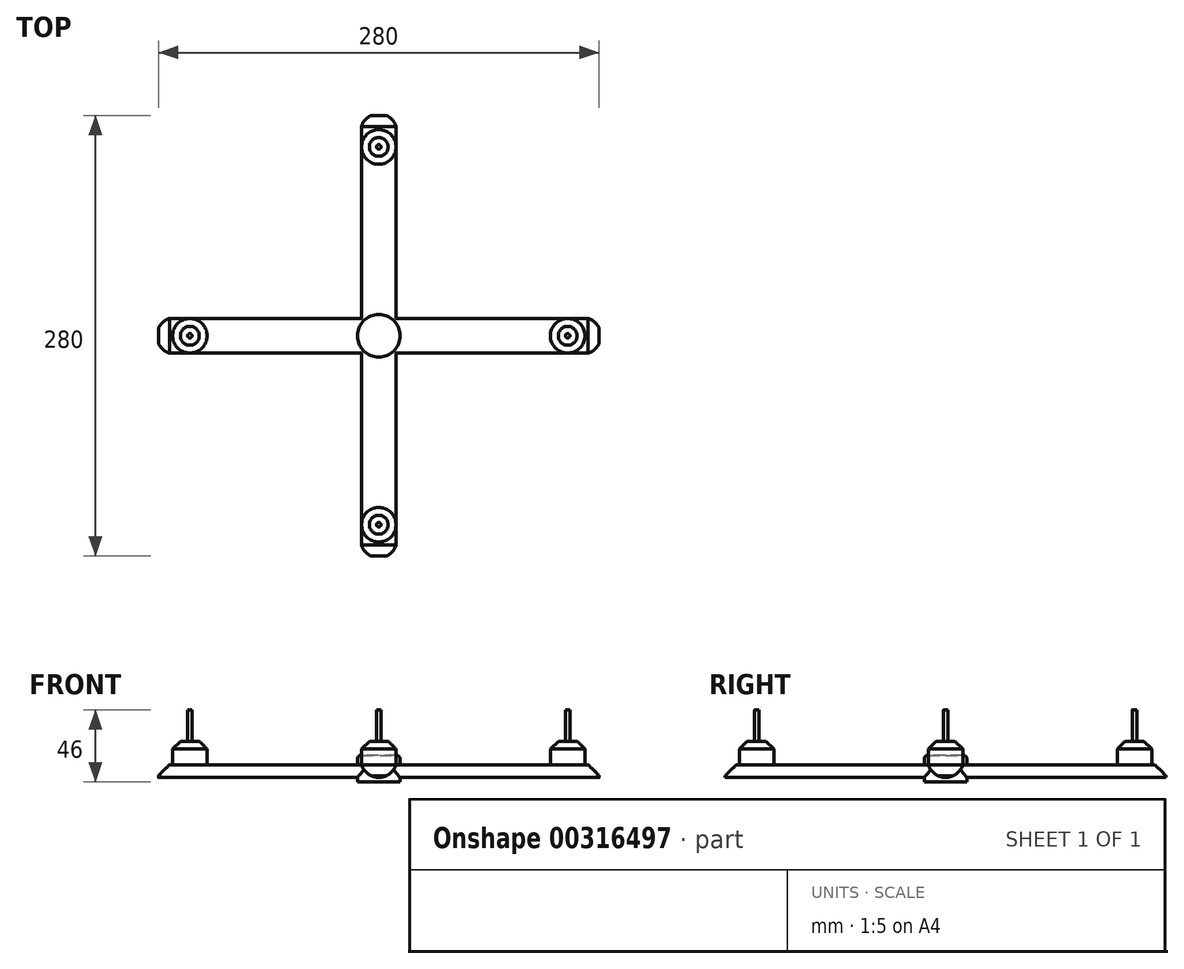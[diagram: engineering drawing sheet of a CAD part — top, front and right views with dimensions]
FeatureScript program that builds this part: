
annotation { "Feature Type Name" : "Feature", "Feature Type Description" : "" }
export const myFeature = defineFeature(function(context is Context, id is Id, definition is map)
    precondition{}
    {
        {
            var Q0;
            Q0=qCreatedBy(makeId("Top.planeOp"),FACE);
            var sketch = newSketch(context, id + "F0", { "sketchPlane" : qUnion([Q0])});
            skCircle(sketch, "E0", {"center": v(0, 0) * mm, "radius": 13.5 * mm});
            skSolve(sketch);
        }
        {
            var Q0;
            Q0=qCreatedBy(makeId("Front.planeOp"),FACE);
            var sketch = newSketch(context, id + "F1", { "sketchPlane" : qUnion([Q0])});
            skLineSegment(sketch, "E1.bottom", {"start": v(-11, 4) * mm, "end": v(11, 4) * mm});
            skLineSegment(sketch, "E1.top", {"start": v(-11, -4) * mm, "end": v(11, -4) * mm});
            skLineSegment(sketch, "E1.left", {"start": v(-11, 4) * mm, "end": v(-11, -4) * mm});
            skLineSegment(sketch, "E1.right", {"start": v(11, 4) * mm, "end": v(11, -4) * mm});
            skPoint(sketch, "E1.middle", {"position": v(0, 0) * mm});
            skSolve(sketch);
        }
        {
            var Q0;
            Q0=qCreatedBy(makeId("Right.planeOp"),FACE);
            var sketch = newSketch(context, id + "F2", { "sketchPlane" : qUnion([Q0])});
            skLineSegment(sketch, "E2.bottom", {"start": v(-11, 4) * mm, "end": v(11, 4) * mm});
            skLineSegment(sketch, "E2.top", {"start": v(-11, -4) * mm, "end": v(11, -4) * mm});
            skLineSegment(sketch, "E2.left", {"start": v(-11, 4) * mm, "end": v(-11, -4) * mm});
            skLineSegment(sketch, "E2.right", {"start": v(11, 4) * mm, "end": v(11, -4) * mm});
            skPoint(sketch, "E2.middle", {"position": v(0, 0) * mm});
            skSolve(sketch);
        }
        {
            var Q0;
            Q0=makeQuery(id+"F2.imprint","IMPRINT",FACE,{"disambiguationData":[TD([[makeQuery(id+"F2.imprint","IMPRINT",EDGE,{"derivedFrom":sQuery(id+"F2.wireOp",EDGE,"E2.bottom")}),-1.0]])]});
            extrude(context, id + "F3", {"entities" : qUnion([Q0]), "depth" : 140 * mm});
        }
        {
            var Q0;
            Q0=makeQuery(id+"F0.imprint","IMPRINT",FACE,{"disambiguationData":[TD([[makeQuery(id+"F0.imprint","IMPRINT",EDGE,{"derivedFrom":sQuery(id+"F0.wireOp",EDGE,"E0")}),1.0]])]});
            extrude(context, id + "F4", {"entities" : qUnion([Q0]), "operationType" : NewBodyOperationType.ADD, "depth" : 10 * mm});
        }
        {
            var Q0;
            Q0=makeQuery(id+"F1.imprint","IMPRINT",FACE,{"disambiguationData":[TD([[makeQuery(id+"F1.imprint","IMPRINT",EDGE,{"derivedFrom":sQuery(id+"F1.wireOp",EDGE,"E1.bottom")}),-1.0]])]});
            extrude(context, id + "F5", {"entities" : qUnion([Q0]), "operationType" : NewBodyOperationType.ADD, "depth" : 140 * mm});
        }
        {
            var Q0;
            Q0=makeQuery(id+"F2.imprint","IMPRINT",FACE,{"disambiguationData":[TD([[makeQuery(id+"F2.imprint","IMPRINT",EDGE,{"derivedFrom":sQuery(id+"F2.wireOp",EDGE,"E2.bottom")}),-1.0]])]});
            extrude(context, id + "F6", {"entities" : qUnion([Q0]), "operationType" : NewBodyOperationType.ADD, "depth" : -140 * mm});
        }
        {
            var Q0;
            Q0=makeQuery(id+"F1.imprint","IMPRINT",FACE,{"disambiguationData":[TD([[makeQuery(id+"F1.imprint","IMPRINT",EDGE,{"derivedFrom":sQuery(id+"F1.wireOp",EDGE,"E1.bottom")}),-1.0]])]});
            extrude(context, id + "F7", {"entities" : qUnion([Q0]), "operationType" : NewBodyOperationType.ADD, "depth" : -140 * mm});
        }
        {
            var Q0;
            Q0=makeQuery(id+"F0.imprint","IMPRINT",FACE,{"disambiguationData":[TD([[makeQuery(id+"F0.imprint","IMPRINT",EDGE,{"derivedFrom":sQuery(id+"F0.wireOp",EDGE,"E0")}),1.0]])]});
            extrude(context, id + "F8", {"entities" : qUnion([Q0]), "operationType" : NewBodyOperationType.ADD, "depth" : -7 * mm});
        }
        {
            var Q0;
            Q0=makeQuery(id+"F4.opExtrude","CAP_EDGE",EDGE,{"disambiguationData":[OSD([sQuery(id+"F0.wireOp",EDGE,"E0")])],"isStart":false});
            fillet(context, id + "F9", {"entities" : qUnion([Q0]), "radius" : 2.17 * mm, "tangentPropagation" : true, "allowEdgeOverflow" : false});
        }
        {
            var Q0;
            Q0=makeQuery(id+"F5.opExtrude","SWEPT_EDGE",EDGE,{"disambiguationData":[OSD([sQuery(id+"F1.wireOp",EDGE,"E1.top"),sQuery(id+"F1.wireOp",EDGE,"E1.right")])]});
            var Q1;
            Q1=makeQuery(id+"F5.opExtrude","SWEPT_EDGE",EDGE,{"disambiguationData":[OSD([sQuery(id+"F1.wireOp",EDGE,"E1.top"),sQuery(id+"F1.wireOp",EDGE,"E1.left")])]});
            var Q2;
            Q2=makeQuery(id+"F6.opExtrude","SWEPT_EDGE",EDGE,{"disambiguationData":[OSD([sQuery(id+"F2.wireOp",EDGE,"E2.top"),sQuery(id+"F2.wireOp",EDGE,"E2.left")])]});
            var Q3;
            {var subQ0=sQuery(id+"F2.wireOp",EDGE,"E2.right");var subQ1=sQuery(id+"F2.wireOp",EDGE,"E2.top");Q3=makeQuery(id+"F7.boolean.opBoolean","SPLIT",EDGE,{"disambiguationData":[TD([makeQuery(id+"F7.opExtrude","SWEPT_FACE",FACE,{"disambiguationData":[OSD([sQuery(id+"F1.wireOp",EDGE,"E1.left")])]})])],"derivedFrom":makeQuery(id+"F6.boolean.opBoolean","MERGE",EDGE,{"derivedFrom":[makeQuery(id+"F3.opExtrude","SWEPT_EDGE",EDGE,{"disambiguationData":[OSD([subQ1,subQ0])]}),makeQuery(id+"F6.opExtrude","SWEPT_EDGE",EDGE,{"disambiguationData":[OSD([subQ1,subQ0])]})]})});}
            var Q4;
            Q4=makeQuery(id+"F7.opExtrude","SWEPT_EDGE",EDGE,{"disambiguationData":[OSD([sQuery(id+"F1.wireOp",EDGE,"E1.top"),sQuery(id+"F1.wireOp",EDGE,"E1.left")])]});
            var Q5;
            Q5=makeQuery(id+"F7.opExtrude","SWEPT_EDGE",EDGE,{"disambiguationData":[OSD([sQuery(id+"F1.wireOp",EDGE,"E1.top"),sQuery(id+"F1.wireOp",EDGE,"E1.right")])]});
            var Q6;
            {var subQ1=sQuery(id+"F2.wireOp",EDGE,"E2.right");var subQ2=sQuery(id+"F2.wireOp",EDGE,"E2.top");Q6=makeQuery(id+"F7.boolean.opBoolean","SPLIT",EDGE,{"disambiguationData":[TD([makeQuery(id+"F7.opExtrude","SWEPT_FACE",FACE,{"disambiguationData":[OSD([sQuery(id+"F1.wireOp",EDGE,"E1.right")])]})])],"derivedFrom":makeQuery(id+"F6.boolean.opBoolean","MERGE",EDGE,{"derivedFrom":[makeQuery(id+"F3.opExtrude","SWEPT_EDGE",EDGE,{"disambiguationData":[OSD([subQ2,subQ1])]}),makeQuery(id+"F6.opExtrude","SWEPT_EDGE",EDGE,{"disambiguationData":[OSD([subQ2,subQ1])]})]})});}
            var Q7;
            Q7=makeQuery(id+"F3.opExtrude","SWEPT_EDGE",EDGE,{"disambiguationData":[OSD([sQuery(id+"F2.wireOp",EDGE,"E2.top"),sQuery(id+"F2.wireOp",EDGE,"E2.left")])]});
            fillet(context, id + "F10", {"entities" : qUnion([Q0, Q1, Q2, Q3, Q4, Q5, Q6, Q7]), "radius" : 11.5 * mm, "tangentPropagation" : true, "allowEdgeOverflow" : false});
        }
        {
            var Q0;
            {var subQ0=sQuery(id+"F1.wireOp",EDGE,"E1.bottom");var subQ1=sQuery(id+"F2.wireOp",EDGE,"E2.bottom");Q0=makeQuery(id+"F7.boolean.opBoolean","MERGE",FACE,{"derivedFrom":[makeQuery(id+"F6.boolean.opBoolean","MERGE",FACE,{"derivedFrom":[makeQuery(id+"F5.boolean.opBoolean","MERGE",FACE,{"derivedFrom":[makeQuery(id+"F3.opExtrude","SWEPT_FACE",FACE,{"disambiguationData":[OSD([subQ1])]}),makeQuery(id+"F5.opExtrude","SWEPT_FACE",FACE,{"disambiguationData":[OSD([subQ0])]})]}),makeQuery(id+"F6.opExtrude","SWEPT_FACE",FACE,{"disambiguationData":[OSD([subQ1])]})]}),makeQuery(id+"F7.opExtrude","SWEPT_FACE",FACE,{"disambiguationData":[OSD([subQ0])]})]});}
            var sketch = newSketch(context, id + "F11", { "sketchPlane" : qUnion([Q0])});
            skLineSegment(sketch, "E3", {"start": v(0, -140) * mm, "end": v(0, -120) * mm});
            skLineSegment(sketch, "E4", {"start": v(140, 0) * mm, "end": v(120, 0) * mm});
            skPoint(sketch, "E4.endSnap0", {"position": v(140, 0) * mm});
            skLineSegment(sketch, "E5", {"start": v(0, 140) * mm, "end": v(0, 120) * mm});
            skLineSegment(sketch, "E6", {"start": v(-140, 0) * mm, "end": v(-120, 0) * mm});
            skCircle(sketch, "E7", {"center": v(0, 120) * mm, "radius": 11 * mm});
            skCircle(sketch, "E8", {"center": v(120, 0) * mm, "radius": 11 * mm});
            skCircle(sketch, "E9", {"center": v(0, -120) * mm, "radius": 11 * mm});
            skCircle(sketch, "E10", {"center": v(-120, 0) * mm, "radius": 11 * mm});
            skSolve(sketch);
        }
        {
            var Q0;
            Q0=makeQuery(id+"F5.opExtrude","CAP_EDGE",EDGE,{"disambiguationData":[OSD([sQuery(id+"F1.wireOp",EDGE,"E1.bottom")])],"isStart":false});
            var Q1;
            Q1=makeQuery(id+"F3.opExtrude","CAP_EDGE",EDGE,{"disambiguationData":[OSD([sQuery(id+"F2.wireOp",EDGE,"E2.bottom")])],"isStart":false});
            var Q2;
            Q2=makeQuery(id+"F7.opExtrude","CAP_EDGE",EDGE,{"disambiguationData":[OSD([sQuery(id+"F1.wireOp",EDGE,"E1.bottom")])],"isStart":false});
            var Q3;
            Q3=makeQuery(id+"F6.opExtrude","CAP_EDGE",EDGE,{"disambiguationData":[OSD([sQuery(id+"F2.wireOp",EDGE,"E2.bottom")])],"isStart":false});
            chamfer(context, id + "F12", {"entities" : qUnion([Q0, Q1, Q2, Q3]), "width" : 7 * mm, "tangentPropagation" : true});
        }
        {
            var Q0;
            {var subQ0=sQuery(id+"F11.wireOp",EDGE,"E9");var subQ7=makeQuery(id+"F11.imprint","INTERSECT",VERTEX,{"derivedFrom":[sQuery(id+"F11.wireOp",EDGE,"E3"),subQ0]});Q0=makeQuery(id+"F11.imprint","IMPRINT",FACE,{"disambiguationData":[TD([[makeQuery(id+"F11.imprint","IMPRINT",EDGE,{"disambiguationData":[TD([[subQ7,1.0]])],"derivedFrom":subQ0}),1.0]])]});}
            var Q1;
            {var subQ0=sQuery(id+"F11.wireOp",EDGE,"E8");var subQ1=makeQuery(id+"F11.imprint","INTERSECT",VERTEX,{"derivedFrom":[sQuery(id+"F11.wireOp",EDGE,"E4"),subQ0]});Q1=makeQuery(id+"F11.imprint","IMPRINT",FACE,{"disambiguationData":[TD([[makeQuery(id+"F11.imprint","IMPRINT",EDGE,{"disambiguationData":[TD([[subQ1,1.0]])],"derivedFrom":subQ0}),1.0]])]});}
            var Q2;
            {var subQ0=sQuery(id+"F11.wireOp",EDGE,"E7");var subQ1=makeQuery(id+"F11.imprint","INTERSECT",VERTEX,{"derivedFrom":[sQuery(id+"F11.wireOp",EDGE,"E5"),subQ0]});Q2=makeQuery(id+"F11.imprint","IMPRINT",FACE,{"disambiguationData":[TD([[makeQuery(id+"F11.imprint","IMPRINT",EDGE,{"disambiguationData":[TD([[subQ1,1.0]])],"derivedFrom":subQ0}),1.0]])]});}
            var Q3;
            {var subQ0=sQuery(id+"F11.wireOp",EDGE,"E10");var subQ1=makeQuery(id+"F11.imprint","INTERSECT",VERTEX,{"derivedFrom":[sQuery(id+"F11.wireOp",EDGE,"E6"),subQ0]});Q3=makeQuery(id+"F11.imprint","IMPRINT",FACE,{"disambiguationData":[TD([[makeQuery(id+"F11.imprint","IMPRINT",EDGE,{"disambiguationData":[TD([[subQ1,-1.0]])],"derivedFrom":subQ0}),1.0]])]});}
            extrude(context, id + "F13", {"entities" : qUnion([Q0, Q1, Q2, Q3]), "operationType" : NewBodyOperationType.ADD, "depth" : 15 * mm});
        }
        {
            var Q0;
            Q0=makeQuery(id+"F13.opExtrude","CAP_EDGE",EDGE,{"disambiguationData":[OSD([sQuery(id+"F11.wireOp",EDGE,"E9")])],"isStart":false});
            var Q1;
            Q1=makeQuery(id+"F13.opExtrude","CAP_EDGE",EDGE,{"disambiguationData":[OSD([sQuery(id+"F11.wireOp",EDGE,"E8")])],"isStart":false});
            var Q2;
            Q2=makeQuery(id+"F13.opExtrude","CAP_EDGE",EDGE,{"disambiguationData":[OSD([sQuery(id+"F11.wireOp",EDGE,"E7")])],"isStart":false});
            var Q3;
            Q3=makeQuery(id+"F13.opExtrude","CAP_EDGE",EDGE,{"disambiguationData":[OSD([sQuery(id+"F11.wireOp",EDGE,"E10")])],"isStart":false});
            chamfer(context, id + "F14", {"entities" : qUnion([Q0, Q1, Q2, Q3]), "width" : 5 * mm, "tangentPropagation" : true});
        }
        {
            var Q0;
            Q0=makeQuery(id+"F13.opExtrude","CAP_FACE",FACE,{"disambiguationData":[OSD([sQuery(id+"F11.wireOp",EDGE,"E8")])],"isStart":false});
            var sketch = newSketch(context, id + "F15", { "sketchPlane" : qUnion([Q0])});
            skCircle(sketch, "E11", {"center": v(120, 0) * mm, "radius": 1.38 * mm});
            skSolve(sketch);
        }
        {
            var Q0;
            Q0=makeQuery(id+"F13.opExtrude","CAP_FACE",FACE,{"disambiguationData":[OSD([sQuery(id+"F11.wireOp",EDGE,"E9")])],"isStart":false});
            var sketch = newSketch(context, id + "F16", { "sketchPlane" : qUnion([Q0])});
            skCircle(sketch, "E12", {"center": v(0, -120) * mm, "radius": 1.38 * mm});
            skSolve(sketch);
        }
        {
            var Q0;
            Q0=makeQuery(id+"F13.opExtrude","CAP_FACE",FACE,{"disambiguationData":[OSD([sQuery(id+"F11.wireOp",EDGE,"E10")])],"isStart":false});
            var sketch = newSketch(context, id + "F17", { "sketchPlane" : qUnion([Q0])});
            skCircle(sketch, "E13", {"center": v(-120, 0) * mm, "radius": 1.38 * mm});
            skSolve(sketch);
        }
        {
            var Q0;
            Q0=makeQuery(id+"F13.opExtrude","CAP_FACE",FACE,{"disambiguationData":[OSD([sQuery(id+"F11.wireOp",EDGE,"E7")])],"isStart":false});
            var sketch = newSketch(context, id + "F18", { "sketchPlane" : qUnion([Q0])});
            skCircle(sketch, "E14", {"center": v(0, 120) * mm, "radius": 1.38 * mm});
            skSolve(sketch);
        }
        {
            var Q0;
            Q0=makeQuery(id+"F15.imprint","IMPRINT",FACE,{"disambiguationData":[TD([[makeQuery(id+"F15.imprint","IMPRINT",EDGE,{"derivedFrom":sQuery(id+"F15.wireOp",EDGE,"E11")}),1.0]])]});
            var Q1;
            Q1=makeQuery(id+"F16.imprint","IMPRINT",FACE,{"disambiguationData":[TD([[makeQuery(id+"F16.imprint","IMPRINT",EDGE,{"derivedFrom":sQuery(id+"F16.wireOp",EDGE,"E12")}),1.0]])]});
            var Q2;
            Q2=makeQuery(id+"F17.imprint","IMPRINT",FACE,{"disambiguationData":[TD([[makeQuery(id+"F17.imprint","IMPRINT",EDGE,{"derivedFrom":sQuery(id+"F17.wireOp",EDGE,"E13")}),1.0]])]});
            var Q3;
            Q3=makeQuery(id+"F18.imprint","IMPRINT",FACE,{"disambiguationData":[TD([[makeQuery(id+"F18.imprint","IMPRINT",EDGE,{"derivedFrom":sQuery(id+"F18.wireOp",EDGE,"E14")}),1.0]])]});
            extrude(context, id + "F19", {"entities" : qUnion([Q0, Q1, Q2, Q3]), "operationType" : NewBodyOperationType.ADD, "depth" : 20 * mm});
        }
    });
